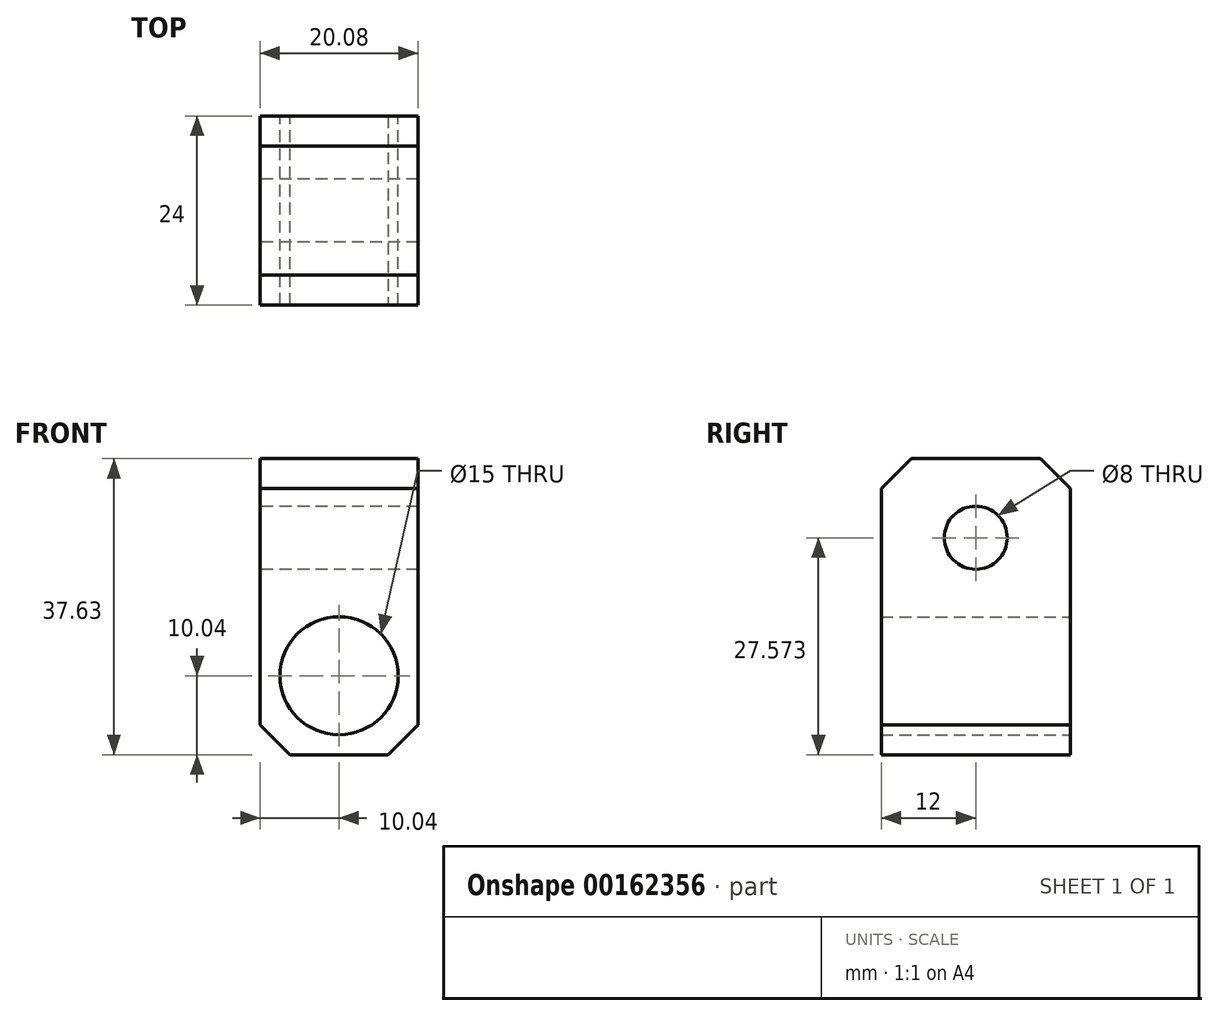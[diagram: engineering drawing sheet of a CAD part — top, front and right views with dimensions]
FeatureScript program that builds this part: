
annotation { "Feature Type Name" : "Feature", "Feature Type Description" : "" }
export const myFeature = defineFeature(function(context is Context, id is Id, definition is map)
    precondition{}
    {
        {
            var Q0;
            Q0=qCreatedBy(makeId("Front.planeOp"),FACE);
            var sketch = newSketch(context, id + "F0", { "sketchPlane" : qUnion([Q0])});
            skLineSegment(sketch, "E0.bottom", {"start": v(0, 0) * mm, "end": v(20.08, 0) * mm});
            skLineSegment(sketch, "E0.top", {"start": v(0, 37.63) * mm, "end": v(20.08, 37.63) * mm});
            skLineSegment(sketch, "E0.left", {"start": v(0, 0) * mm, "end": v(0, 37.63) * mm});
            skLineSegment(sketch, "E0.right", {"start": v(20.08, 0) * mm, "end": v(20.08, 37.63) * mm});
            skCircle(sketch, "E1", {"center": v(10.04, 10.04) * mm, "radius": 7.5 * mm});
            skLineSegment(sketch, "E2", {"start": v(10.04, 10.04) * mm, "end": v(0, 10.04) * mm, "construction": true});
            skLineSegment(sketch, "E3", {"start": v(10.04, 10.04) * mm, "end": v(20.08, 10.04) * mm});
            skLineSegment(sketch, "E4", {"start": v(10.04, 0) * mm, "end": v(10.04, 17.54) * mm});
            skCircle(sketch, "E5", {"center": v(10.04, 27.59) * mm, "radius": 4 * mm});
            skLineSegment(sketch, "E6", {"start": v(10.04, 27.59) * mm, "end": v(0, 27.59) * mm, "construction": true});
            skLineSegment(sketch, "E7", {"start": v(10.04, 27.59) * mm, "end": v(20.08, 27.59) * mm, "construction": true});
            skLineSegment(sketch, "E8", {"start": v(10.04, 27.59) * mm, "end": v(10.04, 17.54) * mm});
            skCircle(sketch, "E9", {"center": v(10.04, 27.59) * mm, "radius": 7.5 * mm});
            skSolve(sketch);
        }
        {
            var Q0;
            {var subQ1=sQuery(id+"F0.wireOp",EDGE,"E0.top");Q0=makeQuery(id+"F0.imprint","IMPRINT",FACE,{"disambiguationData":[TD([[makeQuery(id+"F0.imprint","IMPRINT",EDGE,{"derivedFrom":subQ1}),-1.0]])]});}
            var Q1;
            Q1=makeQuery(id+"F0.imprint","IMPRINT",FACE,{"disambiguationData":[TD([[makeQuery(id+"F0.imprint","IMPRINT",EDGE,{"derivedFrom":sQuery(id+"F0.wireOp",EDGE,"E5")}),1.0]])]});
            var Q2;
            {var subQ1=sQuery(id+"F0.wireOp",EDGE,"E0.right");var subQ7=sQuery(id+"F0.wireOp",EDGE,"E0.bottom");var subQ8=makeQuery(id+"F0.imprint","INTERSECT",VERTEX,{"derivedFrom":[subQ7,subQ1]});Q2=makeQuery(id+"F0.imprint","IMPRINT",FACE,{"disambiguationData":[TD([[makeQuery(id+"F0.imprint","IMPRINT",EDGE,{"disambiguationData":[TD([[subQ8,1.0]])],"derivedFrom":subQ7}),1.0]])]});}
            var Q3;
            Q3=makeQuery(id+"F0.imprint","IMPRINT",FACE,{"disambiguationData":[TD([[makeQuery(id+"F0.imprint","IMPRINT",EDGE,{"derivedFrom":sQuery(id+"F0.wireOp",EDGE,"E5")}),-1.0]])]});
            extrude(context, id + "F1", {"entities" : qUnion([Q0, Q1, Q2, Q3]), "depth" : 24 * mm});
        }
        {
            var Q0;
            Q0=makeQuery(id+"F1.opExtrude","SWEPT_FACE",FACE,{"disambiguationData":[OSD([sQuery(id+"F0.wireOp",EDGE,"E0.left")])]});
            var sketch = newSketch(context, id + "F2", { "sketchPlane" : qUnion([Q0])});
            skLineSegment(sketch, "E10", {"start": v(0, 0) * mm, "end": v(24, 0) * mm});
            skCircle(sketch, "E11", {"center": v(12, 27.57) * mm, "radius": 4 * mm});
            skLineSegment(sketch, "E12", {"start": v(12, 27.57) * mm, "end": v(0, 27.57) * mm, "construction": true});
            skLineSegment(sketch, "E13", {"start": v(12, 27.57) * mm, "end": v(24, 27.57) * mm, "construction": true});
            skSolve(sketch);
        }
        {
            var Q0;
            Q0=makeQuery(id+"F2.imprint","IMPRINT",FACE,{"disambiguationData":[TD([[makeQuery(id+"F2.imprint","IMPRINT",EDGE,{"derivedFrom":sQuery(id+"F2.wireOp",EDGE,"E11")}),1.0]])]});
            extrude(context, id + "F3", {"entities" : qUnion([Q0]), "operationType" : NewBodyOperationType.REMOVE, "oppositeDirection" : true, "depth" : 25.4 * mm});
        }
        {
            var Q0;
            Q0=makeQuery(id+"F1.opExtrude","CAP_EDGE",EDGE,{"disambiguationData":[OSD([sQuery(id+"F0.wireOp",EDGE,"E0.top")])],"isStart":true});
            var Q1;
            Q1=makeQuery(id+"F1.opExtrude","SWEPT_EDGE",EDGE,{"disambiguationData":[OSD([sQuery(id+"F0.wireOp",EDGE,"E0.bottom"),sQuery(id+"F0.wireOp",EDGE,"E0.left")])]});
            var Q2;
            Q2=makeQuery(id+"F1.opExtrude","CAP_EDGE",EDGE,{"disambiguationData":[OSD([sQuery(id+"F0.wireOp",EDGE,"E0.top")])],"isStart":false});
            var Q3;
            Q3=makeQuery(id+"F1.opExtrude","SWEPT_EDGE",EDGE,{"disambiguationData":[OSD([sQuery(id+"F0.wireOp",EDGE,"E0.bottom"),sQuery(id+"F0.wireOp",EDGE,"E0.right")])]});
            chamfer(context, id + "F4", {"entities" : qUnion([Q0, Q1, Q2, Q3]), "width" : 3.8 * mm, "tangentPropagation" : true});
        }
    });
